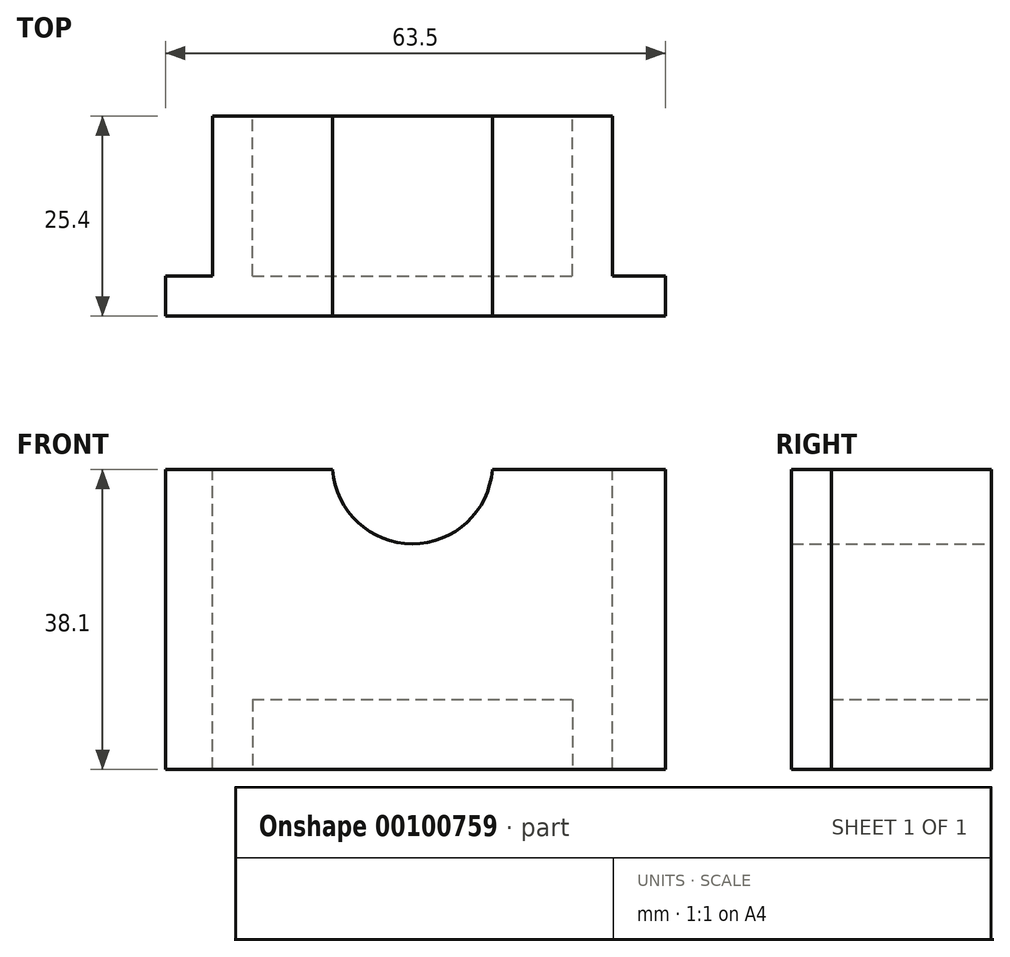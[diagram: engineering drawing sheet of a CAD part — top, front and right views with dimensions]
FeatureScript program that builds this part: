
annotation { "Feature Type Name" : "Feature", "Feature Type Description" : "" }
export const myFeature = defineFeature(function(context is Context, id is Id, definition is map)
    precondition{}
    {
        {
            var Q0;
            Q0=qCreatedBy(makeId("Front.planeOp"),FACE);
            var sketch = newSketch(context, id + "F0", { "sketchPlane" : qUnion([Q0])});
            skLineSegment(sketch, "E0.bottom", {"start": v(-31.64, 19.37) * mm, "end": v(31.86, 19.37) * mm});
            skLineSegment(sketch, "E0.top", {"start": v(-31.64, -18.73) * mm, "end": v(31.86, -18.73) * mm});
            skLineSegment(sketch, "E0.left", {"start": v(-31.64, 19.37) * mm, "end": v(-31.64, -18.73) * mm});
            skLineSegment(sketch, "E0.right", {"start": v(31.86, 19.37) * mm, "end": v(31.86, -18.73) * mm});
            skSolve(sketch);
        }
        {
            var Q0;
            Q0=makeQuery(id+"F0.imprint","IMPRINT",FACE,{"disambiguationData":[TD([[makeQuery(id+"F0.imprint","IMPRINT",EDGE,{"derivedFrom":sQuery(id+"F0.wireOp",EDGE,"E0.bottom")}),-1.0]])]});
            extrude(context, id + "F1", {"entities" : qUnion([Q0]), "depth" : 5.08 * mm});
        }
        {
            var Q0;
            Q0=makeQuery(id+"F1.opExtrude","CAP_FACE",FACE,{"disambiguationData":[OSD([sQuery(id+"F0.wireOp",EDGE,"E0.bottom"),sQuery(id+"F0.wireOp",EDGE,"E0.top"),sQuery(id+"F0.wireOp",EDGE,"E0.left"),sQuery(id+"F0.wireOp",EDGE,"E0.right")])],"isStart":true});
            var sketch = newSketch(context, id + "F2", { "sketchPlane" : qUnion([Q0])});
            skLineSegment(sketch, "E1.bottom", {"start": v(25.7, -18.73) * mm, "end": v(-25.1, -18.73) * mm});
            skLineSegment(sketch, "E1.top", {"start": v(25.7, 19.37) * mm, "end": v(-25.1, 19.37) * mm});
            skLineSegment(sketch, "E1.left", {"start": v(25.7, -18.73) * mm, "end": v(25.7, 19.37) * mm});
            skLineSegment(sketch, "E1.right", {"start": v(-25.1, -18.73) * mm, "end": v(-25.1, 19.37) * mm});
            skSolve(sketch);
        }
        {
            var Q0;
            Q0=makeQuery(id+"F2.imprint","IMPRINT",FACE,{"disambiguationData":[TD([[makeQuery(id+"F2.imprint","IMPRINT",EDGE,{"derivedFrom":sQuery(id+"F2.wireOp",EDGE,"E1.bottom")}),-1.0]])]});
            extrude(context, id + "F3", {"entities" : qUnion([Q0]), "operationType" : NewBodyOperationType.ADD, "depth" : 20.32 * mm});
        }
        {
            var Q0;
            Q0=makeQuery(id+"F3.opExtrude","CAP_FACE",FACE,{"disambiguationData":[OSD([sQuery(id+"F2.wireOp",EDGE,"E1.bottom"),sQuery(id+"F2.wireOp",EDGE,"E1.top"),sQuery(id+"F2.wireOp",EDGE,"E1.left"),sQuery(id+"F2.wireOp",EDGE,"E1.right")])],"isStart":false});
            var sketch = newSketch(context, id + "F4", { "sketchPlane" : qUnion([Q0])});
            skLineSegment(sketch, "E2.bottom", {"start": v(20.61, -9.84) * mm, "end": v(-20.03, -9.84) * mm});
            skLineSegment(sketch, "E2.top", {"start": v(20.61, -18.73) * mm, "end": v(-20.03, -18.73) * mm});
            skLineSegment(sketch, "E2.left", {"start": v(-20.03, -9.84) * mm, "end": v(-20.03, -18.73) * mm});
            skLineSegment(sketch, "E2.right", {"start": v(20.61, -9.84) * mm, "end": v(20.61, -18.73) * mm});
            skSolve(sketch);
        }
        {
            var Q0;
            Q0=makeQuery(id+"F4.imprint","IMPRINT",FACE,{"disambiguationData":[TD([[makeQuery(id+"F4.imprint","IMPRINT",EDGE,{"derivedFrom":sQuery(id+"F4.wireOp",EDGE,"E2.bottom")}),1.0]])]});
            extrude(context, id + "F5", {"entities" : qUnion([Q0]), "operationType" : NewBodyOperationType.REMOVE, "oppositeDirection" : true, "depth" : 20.32 * mm});
        }
        {
            var Q0;
            Q0=makeQuery(id+"F3.opExtrude","CAP_FACE",FACE,{"disambiguationData":[OSD([sQuery(id+"F2.wireOp",EDGE,"E1.bottom"),sQuery(id+"F2.wireOp",EDGE,"E1.top"),sQuery(id+"F2.wireOp",EDGE,"E1.left"),sQuery(id+"F2.wireOp",EDGE,"E1.right")])],"isStart":false});
            var sketch = newSketch(context, id + "F6", { "sketchPlane" : qUnion([Q0])});
            skLineSegment(sketch, "E3", {"start": v(-12.4, 22.12) * mm, "end": v(-12.4, 19.37) * mm});
            skLineSegment(sketch, "E4", {"start": v(13, 19.37) * mm, "end": v(13, 23.76) * mm});
            skLineSegment(sketch, "E5", {"start": v(-32.95, 5.4) * mm, "end": v(35.52, 5.4) * mm});
            skLineSegment(sketch, "E6", {"start": v(-9.87, 19.37) * mm, "end": v(-9.87, 22.24) * mm});
            skLineSegment(sketch, "E7", {"start": v(10.45, 19.37) * mm, "end": v(10.45, 23.69) * mm});
            skArc(sketch, "E8", {"start": v(-9.87, 19.37) * mm, "mid": v(0.3, 9.94) * mm, "end": v(10.45, 19.37) * mm});
            skSolve(sketch);
        }
        {
            var Q0;
            {var subQ0=sQuery(id+"F6.wireOp",EDGE,"E8");Q0=makeQuery(id+"F6.imprint","IMPRINT",FACE,{"disambiguationData":[TD([[makeQuery(id+"F6.imprint","IMPRINT",EDGE,{"derivedFrom":subQ0}),1.0]])]});}
            extrude(context, id + "F7", {"entities" : qUnion([Q0]), "operationType" : NewBodyOperationType.REMOVE, "oppositeDirection" : true, "depth" : 50.8 * mm});
        }
    });
